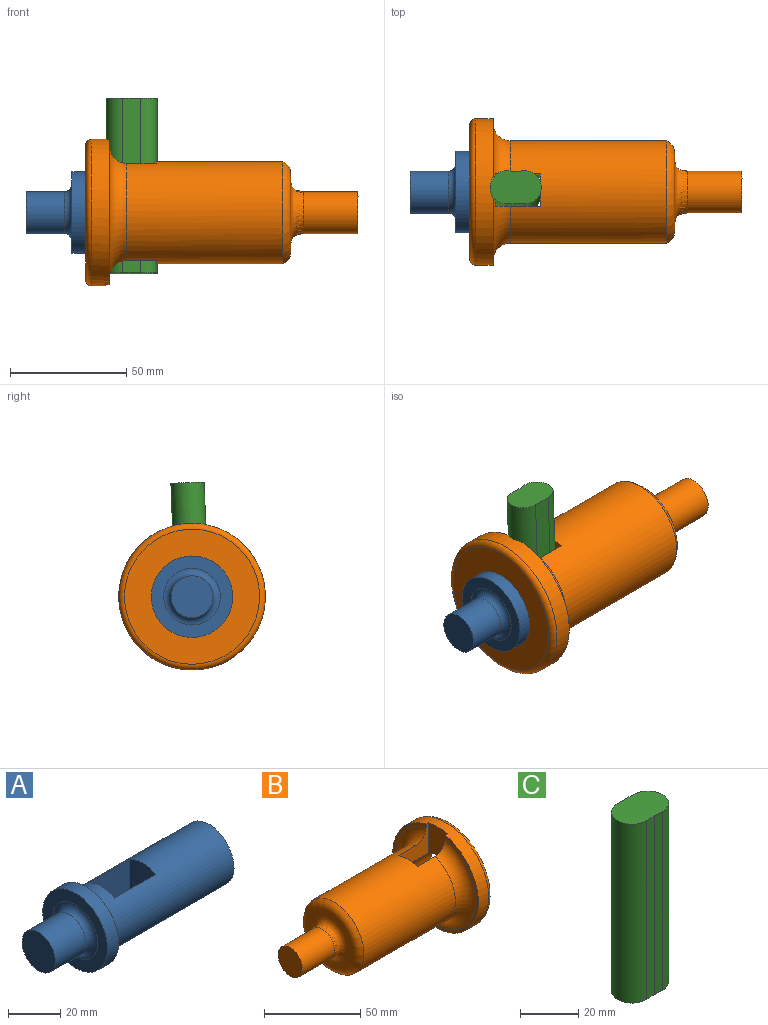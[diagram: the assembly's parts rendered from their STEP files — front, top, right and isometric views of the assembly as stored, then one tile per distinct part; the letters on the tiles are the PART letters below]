
ASSEMBLY  parts=3 mates=3
PART A: 12 faces, bbox 92x35x35 mm
  f0: cylinder r=9mm len=18mm, axis (-1,0,0), area 934.9mm2, adj f1,f6
  f1: plane 18x18mm, normal (-1,0,0), area 254.5mm2, adj f0
  f2: cylinder r=13.5mm len=66.29mm, axis (-1,0,0), area 4975.6mm2, adj f3,f7,f8,f9,f10,f11
  f3: plane 35x35mm, normal (1,0,0), area 389.6mm2, adj f2,f4
  f4: cylinder r=17.5mm len=35mm, axis (-1,0,0), area 659.7mm2, adj f3,f5
  f5: plane 35x35mm, normal (-1,0,0), area 496.6mm2, adj f4,f6
  f6: torus R=12.17mm, axis (-1,0,0), area 318mm2, adj f0,f5
  f7: plane 27x14mm, normal (1,0,0), area 360.3mm2, adj f2,f8,f10
  f8: plane 23.09x22mm, normal (0,1,0), area 507.9mm2, adj f2,f7,f9
  f9: plane 27x14mm, normal (-1,0,0), area 360.3mm2, adj f2,f8,f10
  f10: plane 23.09x22mm, normal (0,-1,0), area 507.9mm2, adj f2,f7,f9
  f11: plane 27x27mm, normal (1,0,0), area 572.6mm2, adj f2
PART B: 20 faces, bbox 116.9x75.4x74.3 mm
  f0: cylinder r=31.5mm len=63mm, axis (-1,0,0), area 1460.3mm2, adj f1,f8,f11,f12,f14
  f1: plane 63x62.21mm, normal (-1,0,0), area 355mm2, adj f0,f2,f11,f12
  f2: torus R=29.5mm, axis (-1,0,0), area 1558.4mm2, adj f1,f3,f11,f12,f16,f17,f19
  f3: cylinder r=22mm len=67.2mm, axis (-1,0,0), area 8924.4mm2, adj f2,f9,f11,f12,f13,f15,f16,f17
  f4: plane 18x18mm, normal (-1,0,0), area 254.5mm2, adj f10
  f5: plane 27x27mm, normal (1,0,0), area 572.6mm2, adj f6
  f6: cylinder r=13.5mm len=79mm, axis (-1,0,0), area 6053.4mm2, adj f5,f7,f11,f12,f13,f14,f15,f16
  f7: plane 58x58mm, normal (1,0,0), area 2069.5mm2, adj f6,f8
  f8: torus R=29mm, axis (-1,0,0), area 754.8mm2, adj f0,f7
  f9: revolved ~44x44mm, area 1643.4mm2, adj f3,f10
  f10: cylinder r=9mm len=23.54mm, axis (-1,0,0), area 1331mm2, adj f4,f9
  f11: plane 22x19.17mm, normal (0,-1,0), area 234.4mm2, adj f0,f1,f2,f3,f6,f13,f14
  f12: plane 22x19.17mm, normal (0,1,0), area 234.4mm2, adj f0,f1,f2,f3,f6,f13,f14
  f13: plane 14x10.46mm, normal (1,0,0), area 122.6mm2, adj f3,f6,f11,f12
  f14: plane 19.96x14mm, normal (-1,0,0), area 257.2mm2, adj f0,f6,f11,f12
  f15: plane 14x10.46mm, normal (1,0,0), area 122.6mm2, adj f3,f6,f16,f17
  f16: plane 22x13.46mm, normal (0,1,0), area 223.6mm2, adj f2,f3,f6,f15,f18,f19
  f17: plane 22x13.46mm, normal (0,-1,0), area 223.6mm2, adj f2,f3,f6,f15,f18,f19
  f18: plane 14x13.46mm, normal (-1,0,0), area 169.8mm2, adj f6,f16,f17,f19
  f19: plane 14.01x3.21mm, normal (0,0,1), area 41.9mm2, adj f2,f16,f17,f18
PART C: 7 faces, bbox 22x14.3x75 mm
  f0: plane 75x7.71mm, normal (0,1,0), area 578.3mm2, adj f1,f4,f5,f6
  f1: cylinder r=7.15mm len=75mm, axis (0,0,-1), area 1684mm2, adj f0,f2,f5,f6
  f2: plane 75x3.86mm, normal (0.08,-1,0), area 290mm2, adj f1,f3,f5,f6
  f3: plane 75x3.86mm, normal (-0.08,-1,0), area 290mm2, adj f2,f4,f5,f6
  f4: cylinder r=7.15mm len=75mm, axis (0,0,-1), area 1684mm2, adj f0,f3,f5,f6
  f5: plane 22.01x14.29mm, normal (0,0,1), area 269.6mm2, adj f0,f1,f2,f3,f4
  f6: plane 22.01x14.29mm, normal (0,0,-1), area 269.6mm2, adj f0,f1,f2,f3,f4
PLACE A rot(axis=(-1,0,0),2.1deg) t=(-56.05,-40.69,-9.01)mm
PLACE B rot(axis=(0,-1,0.02),180deg) t=(0.57,-40.69,-9.01)mm
PLACE C rot(axis=(1,0,0),177.9deg) t=(-58.74,-38.57,39.98)mm
MATE planar B.f0 <-> A.f0  axis (-1,0,0) through (-78.43,-40.69,-9.01)mm
MATE cylindrical A.f0 <-> B.f0  axis (-1,0,0) through (-45.28,-40.69,-9.01)mm
MATE pin_slot C.f0 <-> A.f8  axis (0,-1,0.04) through (-58.74,-47.27,2.78)mm
